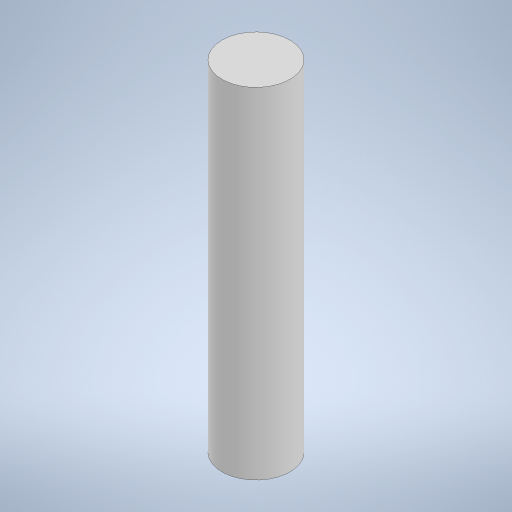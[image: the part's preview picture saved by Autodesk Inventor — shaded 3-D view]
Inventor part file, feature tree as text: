
AUTODESK INVENTOR PART (.ipt)
format: ipt  version: 2023 (Build 270158000, 158)  size: 215,552 bytes
history: native  units: in
note: dims shown in document units (in); Inventor stores cm internally (conversion verified against a paired STEP export)
features: extrude x1, sketch x1
ambient origin geometry x8: Origin, YZ Plane, XZ Plane, XY Plane, X Axis, Y Axis, Z Axis, Center Point
bodies: Solid1 (feature_tree)
feature tree (2):
  extrude  "Extrusion1"  Depth=3.937in TaperAngle=0.0deg
  sketch  "Sketch1"  dims[d0=0.7874in d1=3.937in d2=0.0in]
